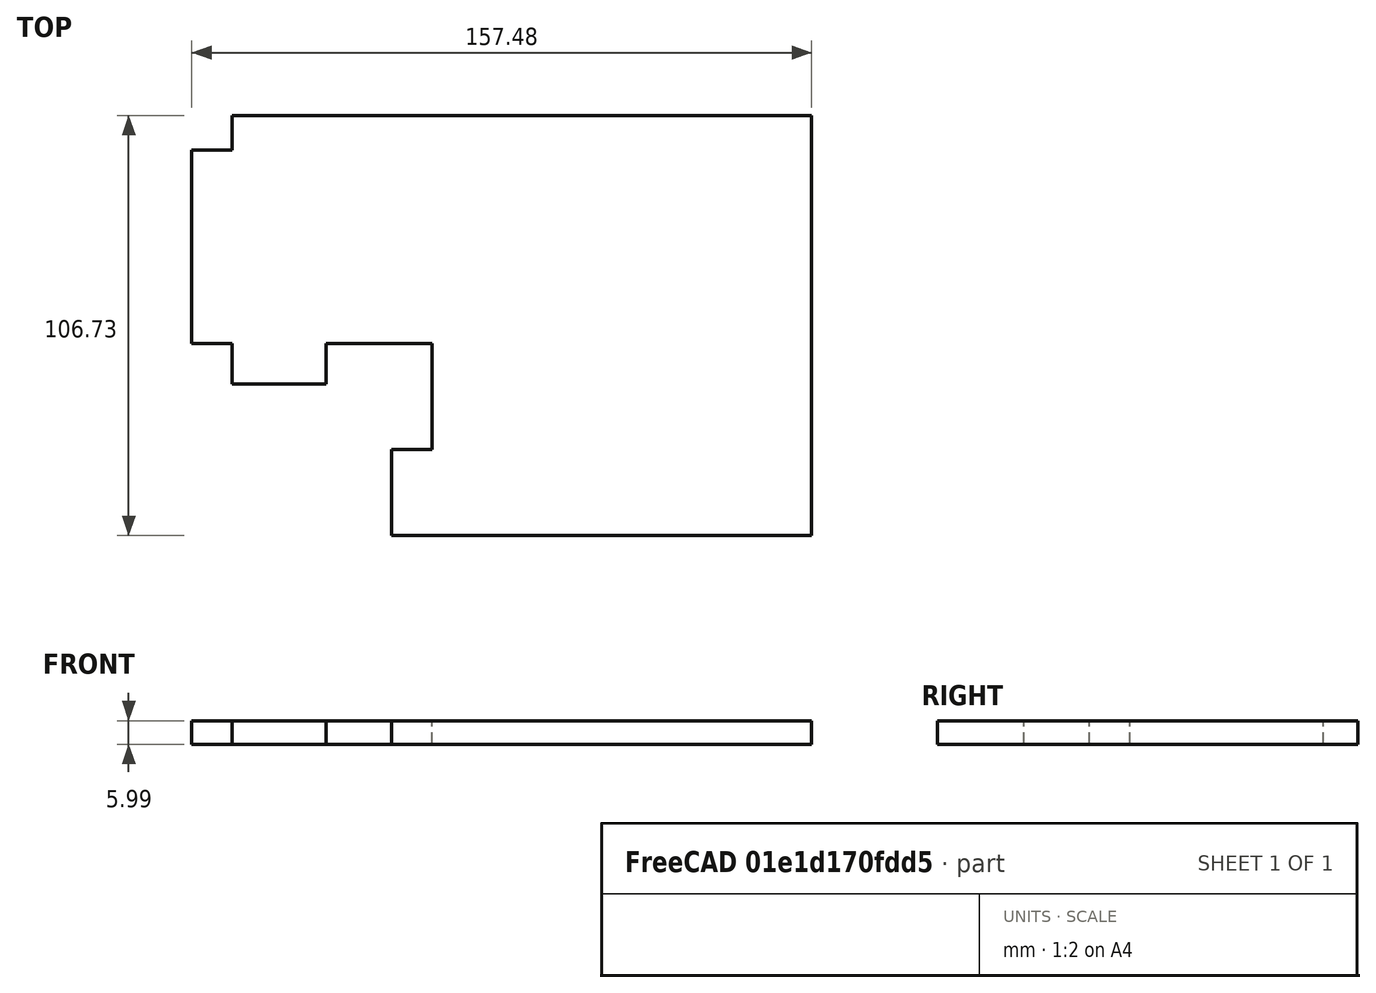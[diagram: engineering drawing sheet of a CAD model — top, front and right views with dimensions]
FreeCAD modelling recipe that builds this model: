
FCSTD DOCUMENT  (FreeCAD 0.19R24267 (Git))
Label: Inv1-P6
License: All rights reserved
LicenseURL: http://en.wikipedia.org/wiki/All_rights_reserved
objects: TechDraw::DrawViewDimension×12, TechDraw::DrawProjGroupItem×2, TechDraw::DrawHatch×2, TechDraw::DrawViewAnnotation×2, Sketcher::SketchObject×1, Part::Extrusion×1, TechDraw::DrawSVGTemplate×1, TechDraw::DrawProjGroup×1, TechDraw::DrawPage×1
note: 2 computed .brp shape members not serialized (recipe doc carries the construction recipe); baked Part::Feature solids carry a one-line shape summary decoded from their .brp

FEATURE [Sketcher::SketchObject] Sketch
  FullyConstrained = true
  sketch-geometry (14):
    g0: LineSegment StartX=-157.48 StartY=-8.7122 StartZ=0 EndX=-147.193 EndY=-8.7122 EndZ=0
    g1: LineSegment StartX=-147.193 StartY=-8.7122 StartZ=0 EndX=-147.193 EndY=0 EndZ=0
    g2: LineSegment StartX=-147.193 StartY=0 StartZ=0 EndX=0 EndY=0 EndZ=0
    g3: LineSegment StartX=-157.48 StartY=-8.7122 StartZ=0 EndX=-157.48 EndY=-57.912 EndZ=0
    g4: LineSegment StartX=-157.48 StartY=-57.912 StartZ=0 EndX=-147.193 EndY=-57.912 EndZ=0
    g5: LineSegment StartX=-147.193 StartY=-57.912 StartZ=0 EndX=-147.193 EndY=-68.199 EndZ=0
    g6: LineSegment StartX=-147.193 StartY=-68.199 StartZ=0 EndX=-123.317 EndY=-68.199 EndZ=0
    g7: LineSegment StartX=-123.317 StartY=-68.199 StartZ=0 EndX=-123.317 EndY=-57.912 EndZ=0
    g8: LineSegment StartX=-123.317 StartY=-57.912 StartZ=0 EndX=-96.393 EndY=-57.912 EndZ=0
    g9: LineSegment StartX=-96.393 StartY=-57.912 StartZ=0 EndX=-96.393 EndY=-84.836 EndZ=0
    g10: LineSegment StartX=-96.393 StartY=-84.836 StartZ=0 EndX=-106.68 EndY=-84.836 EndZ=0
    g11: LineSegment StartX=-106.68 StartY=-84.836 StartZ=0 EndX=-106.68 EndY=-106.731 EndZ=0
    g12: LineSegment StartX=-106.68 StartY=-106.731 StartZ=0 EndX=0 EndY=-106.731 EndZ=0
    g13: LineSegment StartX=0 StartY=-106.731 StartZ=0 EndX=0 EndY=0 EndZ=0
  constraints (41):
    c: Horizontal(g0)
    c: Coincident(g1,g0)
    c: Vertical(g1)
    c: Coincident(g2,g1)
    c: Horizontal(g2)
    c: Coincident(g3,g0)
    c: Vertical(g3)
    c: Coincident(g4,g3)
    c: Horizontal(g4)
    c: Coincident(g5,g4)
    c: Vertical(g5)
    c: Coincident(g6,g5)
    c: Horizontal(g6)
    c: Coincident(g7,g6)
    c: Vertical(g7)
    c: Coincident(g8,g7)
    c: Horizontal(g8)
    c: Coincident(g9,g8)
    c: Vertical(g9)
    c: Coincident(g10,g9)
    c: Horizontal(g10)
    c: Coincident(g11,g10)
    c: Vertical(g11)
    c: Coincident(g12,g11)
    c: Horizontal(g12)
    c: Coincident(g13,g12)
    c: Vertical(g13)
    c: Coincident(g2,g13)
    c: Distance(g2,g3) = 157.48
    c: Distance(g13) = 106.731
    c: Distance(g0) = 10.287
    c: Equal(g0,g4)
    c: Equal(g5,g0)
    c: Equal(g0,g7)
    c: Equal(g10,g0)
    c: Distance(g1) = 8.7122
    c: Distance(g12) = 106.68
    c: Distance(g11) = 21.8948
    c: Distance(g9) = 26.924
    c: Equal(g9,g8)
    c: Coincident(g2,g-1)
FEATURE [Part::Extrusion] Extrude
  Base = -> Sketch
  Dir = (0,0,1)
  DirMode = 2
  FaceMakerClass = Part::FaceMakerBullseye
  LengthFwd = 5.9944
  LengthRev = 0
  Solid = true
  Symmetric = false
FEATURE [TechDraw::DrawSVGTemplate] Template
  Height = 215.9
  Orientation = 1
  Width = 279.4
FEATURE [TechDraw::DrawProjGroupItem] ProjItem  label="Front"
  CoarseView = false
  Direction = (0,0,1)
  Focus = 100
  HardHidden = false
  IsoCount = 0
  IsoHidden = false
  IsoVisible = false
  LockPosition = true
  Perspective = false
  Rotation = 0
  RotationVector = (-1,0,0)
  Scale = 0.5
  ScaleType = 2
  SeamHidden = false
  SeamVisible = true
  SmoothHidden = false
  SmoothVisible = true
  Source = -> [Extrude]
  Type = 0
  X = 0
  XDirection = (-1,0,0)
  Y = 0
FEATURE [TechDraw::DrawProjGroupItem] ProjItem001  label="Left"
  CoarseView = false
  Direction = (1,0,1e-16)
  Focus = 100
  HardHidden = false
  IsoCount = 0
  IsoHidden = false
  IsoVisible = false
  LockPosition = false
  Perspective = false
  Rotation = 0
  RotationVector = (1,0,0)
  Scale = 0.5
  ScaleType = 2
  SeamHidden = false
  SeamVisible = true
  SmoothHidden = false
  SmoothVisible = true
  Source = -> [Extrude]
  Type = 1
  X = 95.4585
  XDirection = (-1e-16,0,1)
  Y = 0
FEATURE [TechDraw::DrawProjGroup] ProjGroup
  Anchor = -> ProjItem
  AutoDistribute = true
  LockPosition = false
  ProjectionType = 0
  Rotation = 0
  Scale = 0.5
  ScaleType = 2
  Source = -> [Extrude]
  Views = -> [ProjItem,ProjItem001]
  X = 115.022
  Y = 108.654
  spacingX = 15.0114
  spacingY = 15.0114
FEATURE [TechDraw::DrawHatch] Hatch  label="HatchF0"
  HatchPattern = <path>
  Source = -> ProjItem [Face0]
FEATURE [TechDraw::DrawHatch] Hatch001  label="Hatch001F0"
  HatchPattern = <path>
  Source = -> ProjItem001 [Face0]
FEATURE [TechDraw::DrawViewDimension] Dimension
  Arbitrary = false
  ArbitraryTolerances = false
  EqualTolerance = true
  FormatSpec = %.3f
  FormatSpecOverTolerance = %+.3f
  FormatSpecUnderTolerance = %+.3f
  Inverted = false
  LockPosition = false
  MeasureType = 1
  OverTolerance = 0
  References2D = -> [ProjItem001]
  Rotation = 0
  ScaleType = 0
  TheoreticalExact = false
  Type = 1
  UnderTolerance = 0
  X = 26.0366
  Y = 27.0713
FEATURE [TechDraw::DrawViewDimension] Dimension001
  Arbitrary = false
  ArbitraryTolerances = false
  EqualTolerance = true
  FormatSpec = %.3f
  FormatSpecOverTolerance = %+.3f
  FormatSpecUnderTolerance = %+.3f
  Inverted = false
  LockPosition = false
  MeasureType = 1
  OverTolerance = 0
  References2D = -> [ProjItem]
  Rotation = 0
  ScaleType = 0
  TheoreticalExact = false
  Type = 1
  UnderTolerance = 0
  X = 1.56686
  Y = -46.859
FEATURE [TechDraw::DrawViewDimension] Dimension002
  Arbitrary = false
  ArbitraryTolerances = false
  EqualTolerance = true
  FormatSpec = %.3f
  FormatSpecOverTolerance = %+.3f
  FormatSpecUnderTolerance = %+.3f
  Inverted = false
  LockPosition = false
  MeasureType = 1
  OverTolerance = 0
  References2D = -> [ProjItem]
  Rotation = 0
  ScaleType = 0
  TheoreticalExact = false
  Type = 1
  UnderTolerance = 0
  X = 54.101
  Y = -13.2157
FEATURE [TechDraw::DrawViewDimension] Dimension003
  Arbitrary = false
  ArbitraryTolerances = false
  EqualTolerance = true
  FormatSpec = %.3f
  FormatSpecOverTolerance = %+.3f
  FormatSpecUnderTolerance = %+.3f
  Inverted = false
  LockPosition = false
  MeasureType = 1
  OverTolerance = 0
  References2D = -> [ProjItem]
  Rotation = 0
  ScaleType = 0
  TheoreticalExact = false
  Type = 2
  UnderTolerance = 0
  X = 13.5003
  Y = -36.9086
FEATURE [TechDraw::DrawViewDimension] Dimension004
  Arbitrary = false
  ArbitraryTolerances = false
  EqualTolerance = true
  FormatSpec = %.3f
  FormatSpecOverTolerance = %+.3f
  FormatSpecUnderTolerance = %+.3f
  Inverted = false
  LockPosition = false
  MeasureType = 1
  OverTolerance = 0
  References2D = -> [ProjItem]
  Rotation = 0
  ScaleType = 0
  TheoreticalExact = false
  Type = 1
  UnderTolerance = 0
  X = 55.391
  Y = 0.661481
FEATURE [TechDraw::DrawViewDimension] Dimension005
  Arbitrary = false
  ArbitraryTolerances = false
  EqualTolerance = true
  FormatSpec = %.3f
  FormatSpecOverTolerance = %+.3f
  FormatSpecUnderTolerance = %+.3f
  Inverted = false
  LockPosition = false
  MeasureType = 1
  OverTolerance = 0
  References2D = -> [ProjItem]
  Rotation = 0
  ScaleType = 0
  TheoreticalExact = false
  Type = 2
  UnderTolerance = 0
  X = 63.6757
  Y = 20.5131
FEATURE [TechDraw::DrawViewDimension] Dimension006
  Arbitrary = false
  ArbitraryTolerances = false
  EqualTolerance = true
  FormatSpec = %.3f
  FormatSpecOverTolerance = %+.3f
  FormatSpecUnderTolerance = %+.3f
  Inverted = false
  LockPosition = false
  MeasureType = 1
  OverTolerance = 0
  References2D = -> [ProjItem]
  Rotation = 0
  ScaleType = 0
  TheoreticalExact = false
  Type = 1
  UnderTolerance = 0
  X = -3.78118
  Y = -3.76234
FEATURE [TechDraw::DrawViewDimension] Dimension007
  Arbitrary = false
  ArbitraryTolerances = false
  EqualTolerance = true
  FormatSpec = %.3f
  FormatSpecOverTolerance = %+.3f
  FormatSpecUnderTolerance = %+.3f
  Inverted = false
  LockPosition = false
  MeasureType = 1
  OverTolerance = 0
  References2D = -> [ProjItem]
  Rotation = 0
  ScaleType = 0
  TheoreticalExact = false
  Type = 2
  UnderTolerance = 0
  X = -24.8971
  Y = -7.09999
FEATURE [TechDraw::DrawViewDimension] Dimension008
  Arbitrary = false
  ArbitraryTolerances = false
  EqualTolerance = true
  FormatSpec = %.3f
  FormatSpecOverTolerance = %+.3f
  FormatSpecUnderTolerance = %+.3f
  Inverted = false
  LockPosition = false
  MeasureType = 1
  OverTolerance = 0
  References2D = -> [ProjItem]
  Rotation = 0
  ScaleType = 0
  TheoreticalExact = false
  Type = 1
  UnderTolerance = 0
  X = -8.14858
  Y = 24.5854
FEATURE [TechDraw::DrawViewDimension] Dimension009
  Arbitrary = false
  ArbitraryTolerances = false
  EqualTolerance = true
  FormatSpec = %.3f
  FormatSpecOverTolerance = %+.3f
  FormatSpecUnderTolerance = %+.3f
  Inverted = false
  LockPosition = false
  MeasureType = 1
  OverTolerance = 0
  References2D = -> [ProjItem]
  Rotation = 0
  ScaleType = 0
  TheoreticalExact = false
  Type = 2
  UnderTolerance = 0
  X = -20.4593
  Y = 41.1595
FEATURE [TechDraw::DrawViewDimension] Dimension010
  Arbitrary = false
  ArbitraryTolerances = false
  EqualTolerance = true
  FormatSpec = %.3f
  FormatSpecOverTolerance = %+.3f
  FormatSpecUnderTolerance = %+.3f
  Inverted = false
  LockPosition = false
  MeasureType = 1
  OverTolerance = 0
  References2D = -> [ProjItem]
  Rotation = 0
  ScaleType = 0
  TheoreticalExact = false
  Type = 1
  UnderTolerance = 0
  X = 50.1166
  Y = 17.7796
FEATURE [TechDraw::DrawViewAnnotation] Annotation
  Font = osifont
  LineSpace = 80
  LockPosition = false
  MaxWidth = -1
  Rotation = 0
  ScaleType = 0
  Text = Figure S1 (Inverted 1) | Panel 6 [focus knob top right] | Quantity: 1
  TextSize = 5.0038
  TextStyle = 0
  X = 42.1602
  Y = 195.58
FEATURE [TechDraw::DrawViewAnnotation] Annotation002
  Font = osifont
  LineSpace = 80
  LockPosition = false
  MaxWidth = -1
  Rotation = 0
  ScaleType = 0
  Text = Units: Inches
  TextSize = 5.0038
  TextStyle = 0
  X = 259.08
  Y = 5.08
FEATURE [TechDraw::DrawViewDimension] Dimension011
  Arbitrary = false
  ArbitraryTolerances = false
  EqualTolerance = true
  FormatSpec = %.3f
  FormatSpecOverTolerance = %+.3f
  FormatSpecUnderTolerance = %+.3f
  Inverted = false
  LockPosition = false
  MeasureType = 1
  OverTolerance = 0
  References2D = -> [ProjItem]
  Rotation = 0
  ScaleType = 0
  TheoreticalExact = false
  Type = 2
  UnderTolerance = 0
  X = -52.6659
  Y = 0
FEATURE [TechDraw::DrawPage] Page
  KeepUpdated = true
  NextBalloonIndex = 1
  ProjectionType = 0
  Template = -> Template
  Views = -> [ProjGroup,Dimension,Dimension001,Dimension002,Dimension003,Dimension004,Dimension005,Dimension006,Dimension007,Dimension008,Dimension009,Dimension010,Annotation,Annotation002,Dimension011]
note: 2 file-system paths scrubbed to <path> (originals preserved in the JSON sidecar)
